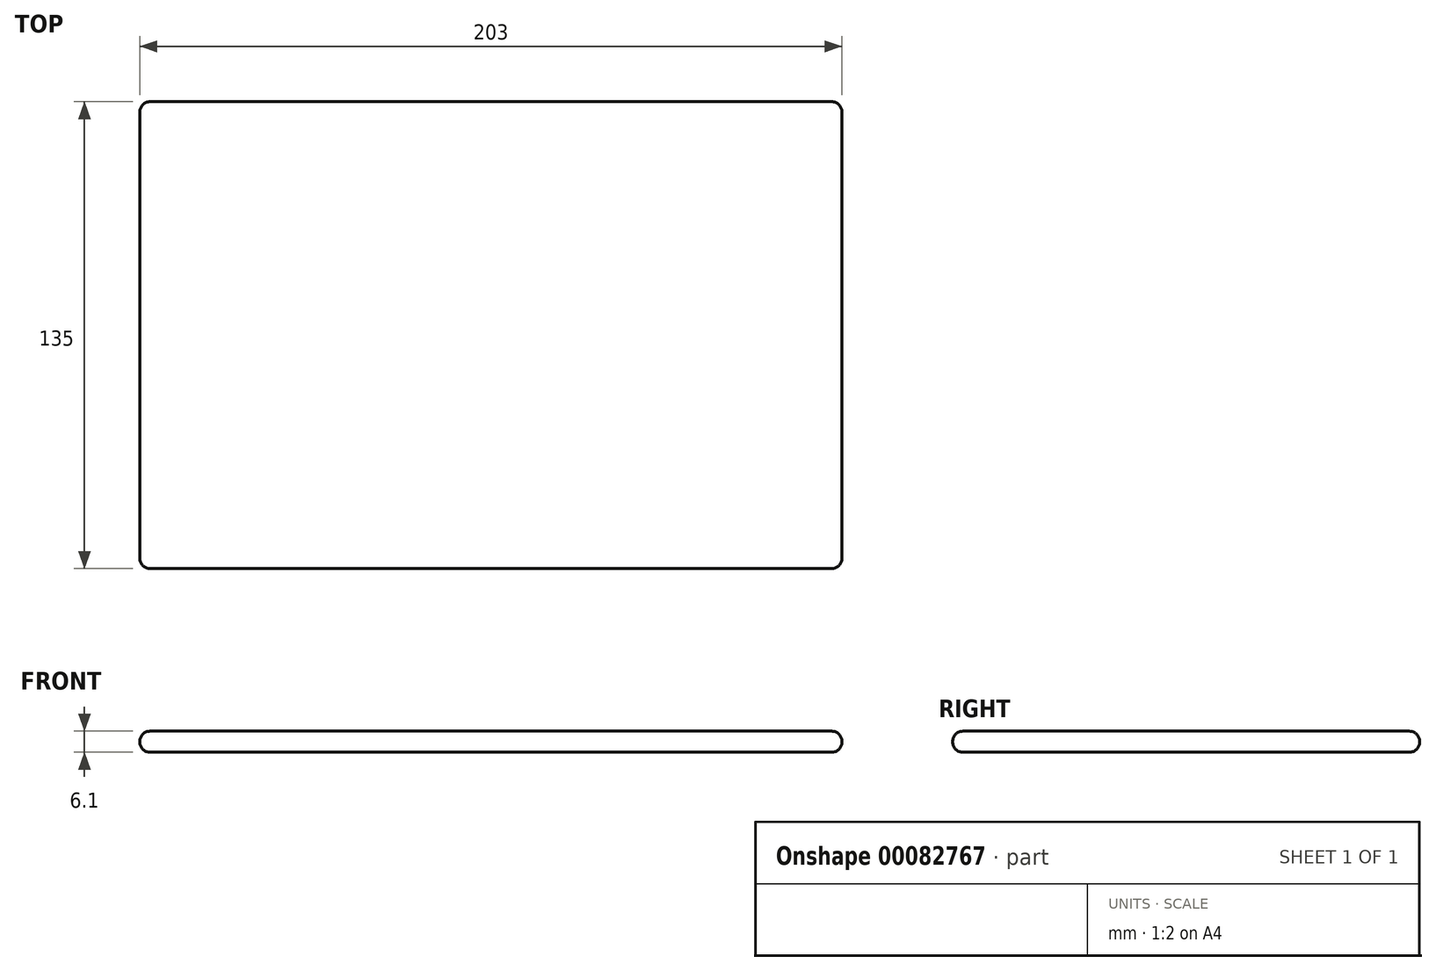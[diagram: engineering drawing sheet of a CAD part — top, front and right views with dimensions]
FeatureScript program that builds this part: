
annotation { "Feature Type Name" : "Feature", "Feature Type Description" : "" }
export const myFeature = defineFeature(function(context is Context, id is Id, definition is map)
    precondition{}
    {
        {
            var Q0;
            Q0=qCreatedBy(makeId("Top.planeOp"),FACE);
            var sketch = newSketch(context, id + "F0", { "sketchPlane" : qUnion([Q0])});
            skLineSegment(sketch, "E0.bottom", {"start": v(101.5, 67.5) * mm, "end": v(-101.5, 67.5) * mm});
            skLineSegment(sketch, "E0.top", {"start": v(101.5, -67.5) * mm, "end": v(-101.5, -67.5) * mm});
            skLineSegment(sketch, "E0.left", {"start": v(101.5, 67.5) * mm, "end": v(101.5, -67.5) * mm});
            skLineSegment(sketch, "E0.right", {"start": v(-101.5, 67.5) * mm, "end": v(-101.5, -67.5) * mm});
            skPoint(sketch, "E0.middle", {"position": v(0, 0) * mm});
            skSolve(sketch);
        }
        {
            var Q0;
            Q0=makeQuery(id+"F0.imprint","IMPRINT",FACE,{"disambiguationData":[TD([[makeQuery(id+"F0.imprint","IMPRINT",EDGE,{"derivedFrom":sQuery(id+"F0.wireOp",EDGE,"E0.bottom")}),1.0]])]});
            extrude(context, id + "F1", {"entities" : qUnion([Q0]), "depth" : 6.1 * mm});
        }
        {
            var Q0;
            Q0=makeQuery(id+"F1.opExtrude","SWEPT_FACE",FACE,{"disambiguationData":[OSD([sQuery(id+"F0.wireOp",EDGE,"E0.bottom")])]});
            var Q1;
            Q1=makeQuery(id+"F1.opExtrude","SWEPT_FACE",FACE,{"disambiguationData":[OSD([sQuery(id+"F0.wireOp",EDGE,"E0.right")])]});
            var Q2;
            Q2=makeQuery(id+"F1.opExtrude","SWEPT_FACE",FACE,{"disambiguationData":[OSD([sQuery(id+"F0.wireOp",EDGE,"E0.top")])]});
            var Q3;
            Q3=makeQuery(id+"F1.opExtrude","SWEPT_FACE",FACE,{"disambiguationData":[OSD([sQuery(id+"F0.wireOp",EDGE,"E0.left")])]});
            fillet(context, id + "F2", {"entities" : qUnion([Q0, Q1, Q2, Q3]), "radius" : 3 * mm, "tangentPropagation" : true, "allowEdgeOverflow" : false});
        }
    });
